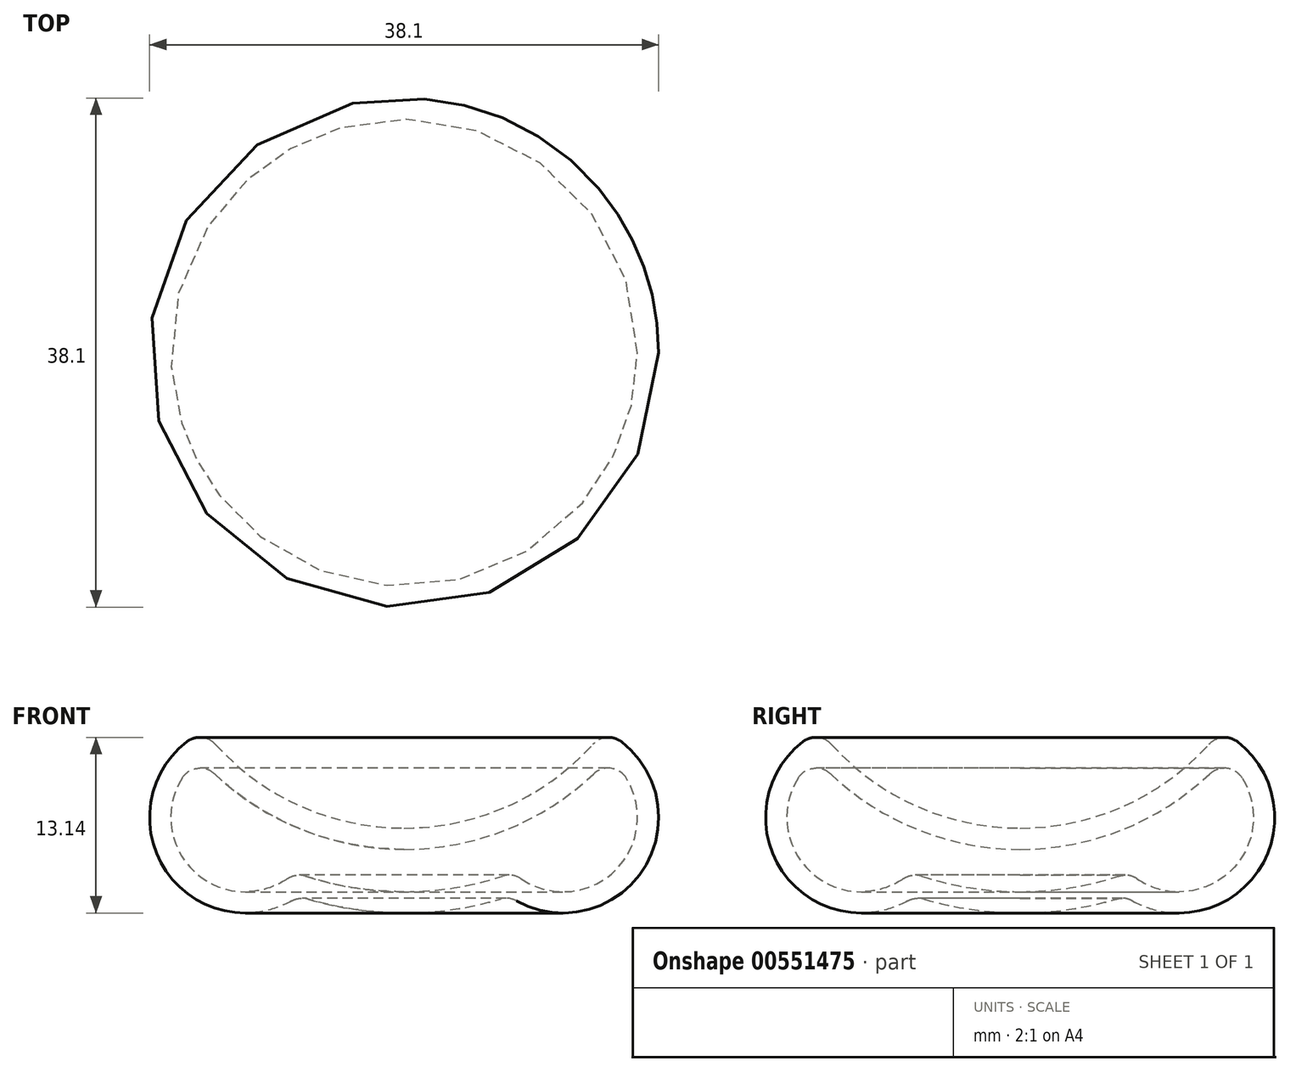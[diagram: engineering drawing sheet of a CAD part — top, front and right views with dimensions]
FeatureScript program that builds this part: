
annotation { "Feature Type Name" : "Feature", "Feature Type Description" : "" }
export const myFeature = defineFeature(function(context is Context, id is Id, definition is map)
    precondition{}
    {
        {
            var Q0;
            Q0=qCreatedBy(makeId("Front.planeOp"),FACE);
            var sketch = newSketch(context, id + "F0", { "sketchPlane" : qUnion([Q0])});
            skArc(sketch, "E0", {"start": v(0, 6.35) * mm, "mid": v(7.73, 7.99) * mm, "end": v(14.13, 12.62) * mm});
            skArc(sketch, "E1", {"start": v(0, 0) * mm, "mid": v(3.63, 0.26) * mm, "end": v(7.2, 1.04) * mm});
            skArc(sketch, "E2", {"start": v(16.27, 12.8) * mm, "mid": v(17.87, 3.21) * mm, "end": v(8.42, 0.9) * mm});
            skLineSegment(sketch, "E3", {"start": v(19.05, 0) * mm, "end": v(19.05, 25.4) * mm, "construction": true});
            skPoint(sketch, "E4.visualSharp", {"position": v(14.97, 13.61) * mm});
            skArc(sketch, "E4.filletArc", {"start": v(16.27, 12.8) * mm, "mid": v(15.16, 13.13) * mm, "end": v(14.13, 12.62) * mm});
            skPoint(sketch, "E5.visualSharp", {"position": v(7.86, 1.25) * mm});
            skArc(sketch, "E5.filletArc", {"start": v(8.42, 0.9) * mm, "mid": v(7.82, 1.1) * mm, "end": v(7.2, 1.04) * mm});
            skLineSegment(sketch, "E6", {"start": v(0, 25.4) * mm, "end": v(16.27, 12.8) * mm, "construction": true});
            skArc(sketch, "E7", {"start": v(0, 4.76) * mm, "mid": v(7.63, 6.23) * mm, "end": v(14.18, 10.4) * mm});
            skArc(sketch, "E8", {"start": v(0, 1.59) * mm, "mid": v(3.73, 1.88) * mm, "end": v(7.37, 2.76) * mm});
            skLineSegment(sketch, "E9", {"start": v(0, 6.35) * mm, "end": v(0, 4.76) * mm});
            skLineSegment(sketch, "E10", {"start": v(0, 1.59) * mm, "end": v(0, 0) * mm});
            skArc(sketch, "E11", {"start": v(16.62, 10.1) * mm, "mid": v(15.75, 3.13) * mm, "end": v(8.76, 2.56) * mm});
            skArc(sketch, "E12.filletArc", {"start": v(16.62, 10.1) * mm, "mid": v(15.48, 10.83) * mm, "end": v(14.18, 10.4) * mm});
            skPoint(sketch, "E13.visualSharp", {"position": v(8.16, 3.03) * mm});
            skArc(sketch, "E13.filletArc", {"start": v(8.76, 2.56) * mm, "mid": v(8.09, 2.82) * mm, "end": v(7.37, 2.76) * mm});
            skSolve(sketch);
        }
        {
            var Q0;
            Q0 = qSketchRegion(id + "F0", true);
            var Q1;
            Q1=sQuery(id+"F0.wireOp",EDGE,"E9");
            revolve(context, id + "F1", {"entities" : qUnion([Q0]), "axis" : qUnion([Q1]), "revolveType" : RevolveType.FULL});
        }
    });
